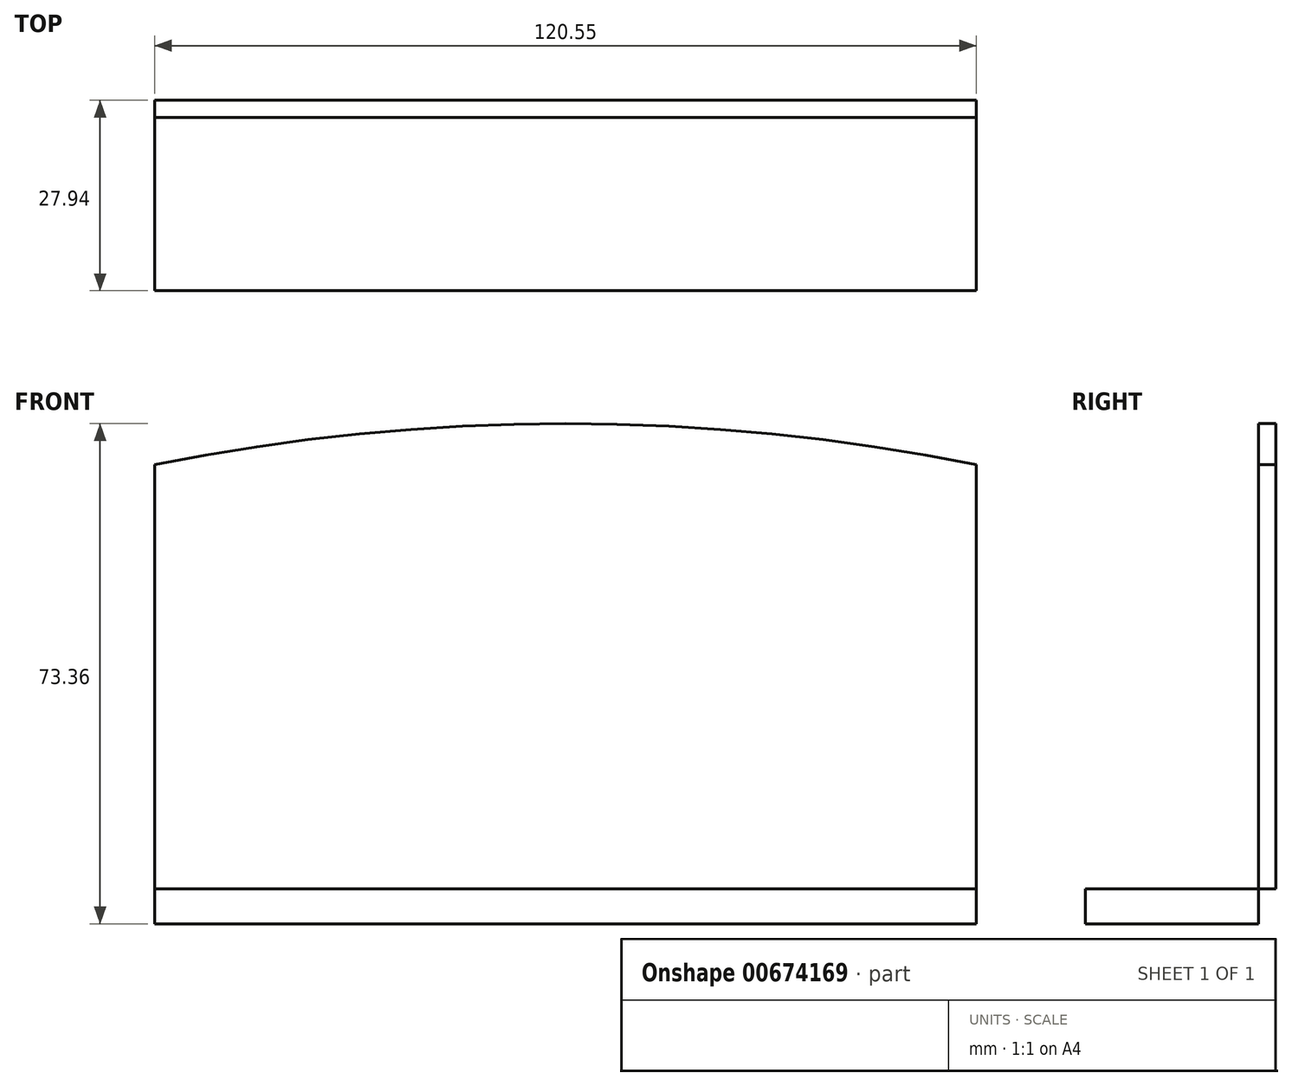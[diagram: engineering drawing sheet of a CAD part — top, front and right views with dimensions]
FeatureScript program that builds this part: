
annotation { "Feature Type Name" : "Feature", "Feature Type Description" : "" }
export const myFeature = defineFeature(function(context is Context, id is Id, definition is map)
    precondition{}
    {
        {
            var Q0;
            Q0=qCreatedBy(makeId("Front.planeOp"),FACE);
            var sketch = newSketch(context, id + "F0", { "sketchPlane" : qUnion([Q0])});
            skLineSegment(sketch, "E0", {"start": v(-46.85, -67.97) * mm, "end": v(73.7, -67.97) * mm});
            skLineSegment(sketch, "E1", {"start": v(73.7, -67.97) * mm, "end": v(73.7, 52.8) * mm});
            skLineSegment(sketch, "E2", {"start": v(73.7, 63.52) * mm, "end": v(-46.85, 63.52) * mm});
            skLineSegment(sketch, "E3", {"start": v(-46.85, 63.52) * mm, "end": v(-105.2, 76.26) * mm});
            skLineSegment(sketch, "E4", {"start": v(-105.2, 76.26) * mm, "end": v(-105.2, -75.61) * mm});
            skLineSegment(sketch, "E5", {"start": v(-105.2, -75.61) * mm, "end": v(97.3, -75.61) * mm});
            skLineSegment(sketch, "E6", {"start": v(97.3, -75.61) * mm, "end": v(97.3, 76.26) * mm});
            skLineSegment(sketch, "E7", {"start": v(97.3, 76.26) * mm, "end": v(-105.2, 76.26) * mm});
            skLineSegment(sketch, "E8", {"start": v(73.7, 63.52) * mm, "end": v(89.77, 76.26) * mm});
            skLineSegment(sketch, "E9", {"start": v(73.7, -67.97) * mm, "end": v(83.9, -75.61) * mm});
            skLineSegment(sketch, "E10", {"start": v(-46.85, 52.8) * mm, "end": v(-46.85, -67.97) * mm});
            skLineSegment(sketch, "E11", {"start": v(-46.85, -67.97) * mm, "end": v(-46.85, -71.07) * mm});
            skLineSegment(sketch, "E12", {"start": v(-46.85, -71.07) * mm, "end": v(73.7, -71.07) * mm});
            skLineSegment(sketch, "E13", {"start": v(73.7, -71.07) * mm, "end": v(73.7, -67.97) * mm});
            skLineSegment(sketch, "E14", {"start": v(73.7, -71.07) * mm, "end": v(79.77, -75.61) * mm});
            skLineSegment(sketch, "E15", {"start": v(-46.85, -67.97) * mm, "end": v(-64.15, -75.61) * mm});
            skLineSegment(sketch, "E16", {"start": v(-46.85, -71.07) * mm, "end": v(-57.14, -75.61) * mm});
            skLineSegment(sketch, "E17", {"start": v(-66.17, -75.61) * mm, "end": v(-66.17, 52.8) * mm});
            skArc(sketch, "E18", {"start": v(-66.17, 52.8) * mm, "mid": v(-84.45, 63.86) * mm, "end": v(-105.2, 68.89) * mm});
            skLineSegment(sketch, "E19", {"start": v(-66.17, 52.8) * mm, "end": v(-75.43, 48.72) * mm});
            skLineSegment(sketch, "E20", {"start": v(-75.43, 48.72) * mm, "end": v(-75.43, -75.61) * mm});
            skArc(sketch, "E21", {"start": v(-75.43, 48.72) * mm, "mid": v(-88.83, 59.45) * mm, "end": v(-105.2, 64.65) * mm});
            skLineSegment(sketch, "E22", {"start": v(-97.64, 43.4) * mm, "end": v(-97.64, -58.27) * mm});
            skLineSegment(sketch, "E23", {"start": v(-97.64, -58.27) * mm, "end": v(-75.43, -52.26) * mm});
            skLineSegment(sketch, "E24", {"start": v(-97.64, -58.27) * mm, "end": v(-97.64, -61.27) * mm});
            skLineSegment(sketch, "E25", {"start": v(-97.64, -61.27) * mm, "end": v(-75.43, -55.26) * mm});
            skLineSegment(sketch, "E26", {"start": v(-97.64, -61.27) * mm, "end": v(-101.07, -59.13) * mm});
            skLineSegment(sketch, "E27", {"start": v(-97.64, -58.27) * mm, "end": v(-101.07, -56.28) * mm});
            skLineSegment(sketch, "E28", {"start": v(-101.07, -56.28) * mm, "end": v(-101.07, -59.13) * mm});
            skLineSegment(sketch, "E29", {"start": v(-101.07, -56.28) * mm, "end": v(-101.07, 48.19) * mm});
            skArc(sketch, "E30", {"start": v(-82.39, 55.3) * mm, "mid": v(-92, 51.91) * mm, "end": v(-97.64, 43.4) * mm});
            skLineSegment(sketch, "E31", {"start": v(-97.64, 43.4) * mm, "end": v(-75.43, 41.06) * mm});
            skLineSegment(sketch, "E32", {"start": v(-101.07, 48.19) * mm, "end": v(-105.2, 48.19) * mm});
            skArc(sketch, "E33", {"start": v(73.7, 52.8) * mm, "mid": v(13.42, 58.84) * mm, "end": v(-46.85, 52.8) * mm});
            skLineSegment(sketch, "E34", {"start": v(-46.85, -14.52) * mm, "end": v(73.7, -14.52) * mm});
            skLineSegment(sketch, "E35", {"start": v(-46.85, -9.38) * mm, "end": v(73.7, -9.38) * mm});
            skSolve(sketch);
        }
        {
            var Q0;
            {var subQ0=sQuery(id+"F0.wireOp",EDGE,"E33");Q0=makeQuery(id+"F0.imprint","IMPRINT",FACE,{"disambiguationData":[TD([[makeQuery(id+"F0.imprint","IMPRINT",EDGE,{"derivedFrom":subQ0}),1.0]])]});}
            extrude(context, id + "F1", {"entities" : qUnion([Q0]), "oppositeDirection" : true, "depth" : 2.54 * mm, "offsetDistance" : 25.4 * mm});
        }
        {
            var Q0;
            {var subQ0=sQuery(id+"F0.wireOp",EDGE,"E34");Q0=makeQuery(id+"F0.imprint","IMPRINT",FACE,{"disambiguationData":[TD([[makeQuery(id+"F0.imprint","IMPRINT",EDGE,{"derivedFrom":subQ0}),1.0]])]});}
            extrude(context, id + "F2", {"entities" : qUnion([Q0]), "operationType" : NewBodyOperationType.ADD, "depth" : 25.4 * mm, "offsetDistance" : 25.4 * mm});
        }
    });
